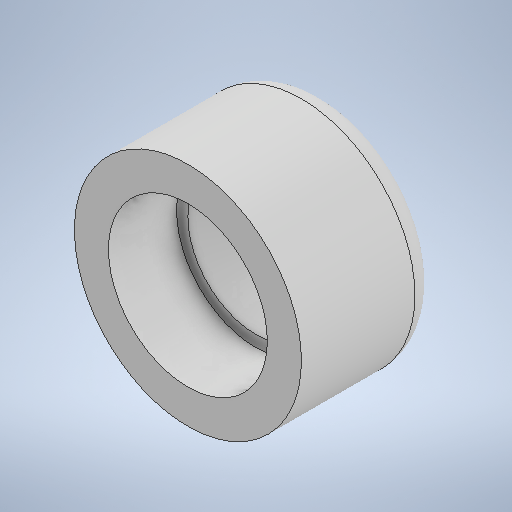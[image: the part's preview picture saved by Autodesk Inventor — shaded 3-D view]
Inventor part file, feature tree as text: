
AUTODESK INVENTOR PART (.ipt)
format: ipt  version: 2025.1 (Build 291241000, 241)  size: 260,608 bytes
history: native  units: mm
features: sketch x2, revolve x1, hole x1, fillet x1
ambient origin geometry x8: Origin, YZ Plane, XZ Plane, XY Plane, X Axis, Y Axis, Z Axis, Center Point
bodies: Solid1 (feature_tree)
feature tree (5):
  revolve  "Revolution1"  [1 undecoded]
  hole  "Hole1"  [1 undecoded]
  fillet  "Fillet1"  [1 undecoded]
  sketch  "Sketch1"  dims[d0=7.0mm d1=10.0mm]
  sketch  "Sketch2"  dims[d2=3.0mm d3=6.0mm d4=90.0deg d5=3.0mm d6=6.0mm d7=6.0mm d8=2.0mm d9=90.0deg d10=8.0mm d11=0.0mm d12=1.0mm]
note: 3 required parameter values undecoded (feature->parameter linkage not recoverable at this tier; creation-order binding heuristic only, values carry confidence <= 0.55)